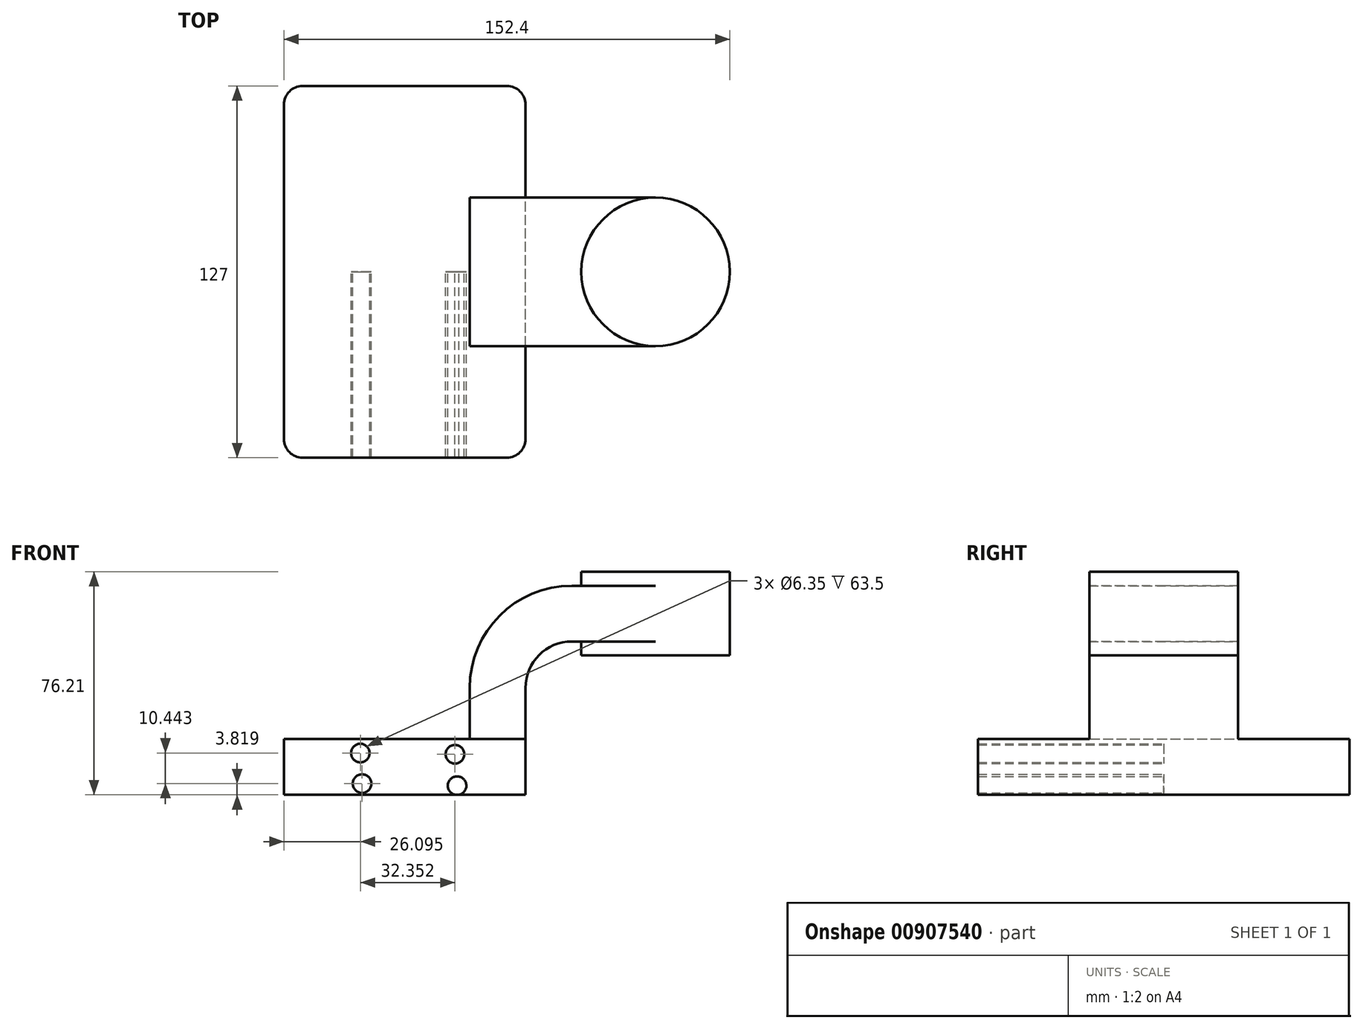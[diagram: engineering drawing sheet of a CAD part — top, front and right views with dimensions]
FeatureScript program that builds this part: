
annotation { "Feature Type Name" : "Feature", "Feature Type Description" : "" }
export const myFeature = defineFeature(function(context is Context, id is Id, definition is map)
    precondition{}
    {
        {
            var Q0;
            Q0=qCreatedBy(makeId("Front.planeOp"),FACE);
            var sketch = newSketch(context, id + "F0", { "sketchPlane" : qUnion([Q0])});
            skLineSegment(sketch, "E0.bottom", {"start": v(41.27, 9.53) * mm, "end": v(-41.28, 9.53) * mm});
            skLineSegment(sketch, "E0.top", {"start": v(41.28, -9.52) * mm, "end": v(-41.27, -9.52) * mm});
            skLineSegment(sketch, "E0.left", {"start": v(41.28, 9.53) * mm, "end": v(41.28, -9.52) * mm});
            skLineSegment(sketch, "E0.right", {"start": v(-41.28, 9.53) * mm, "end": v(-41.27, -9.52) * mm});
            skPoint(sketch, "E0.middle", {"position": v(0, 0) * mm});
            skLineSegment(sketch, "E1.bottom", {"start": v(111.13, 66.68) * mm, "end": v(60.33, 66.68) * mm});
            skLineSegment(sketch, "E1.top", {"start": v(111.13, 38.1) * mm, "end": v(60.33, 38.1) * mm});
            skLineSegment(sketch, "E1.left", {"start": v(111.13, 66.68) * mm, "end": v(111.13, 38.1) * mm});
            skLineSegment(sketch, "E1.right", {"start": v(60.33, 66.68) * mm, "end": v(60.33, 38.1) * mm});
            skPoint(sketch, "E1.middle", {"position": v(85.73, 52.39) * mm});
            skLineSegment(sketch, "E2", {"start": v(41.27, 9.53) * mm, "end": v(41.27, 27) * mm});
            skArc(sketch, "E3", {"start": v(41.27, 27) * mm, "mid": v(45.92, 38.23) * mm, "end": v(57.15, 42.88) * mm});
            skLineSegment(sketch, "E4", {"start": v(57.15, 42.88) * mm, "end": v(85.73, 42.88) * mm});
            skPoint(sketch, "E4.endSnap0", {"position": v(85.73, 38.1) * mm});
            skLineSegment(sketch, "E5.0", {"start": v(57.15, 61.93) * mm, "end": v(85.73, 61.93) * mm});
            skArc(sketch, "E5.1", {"start": v(22.23, 27) * mm, "mid": v(32.45, 51.7) * mm, "end": v(57.15, 61.93) * mm});
            skLineSegment(sketch, "E5.2", {"start": v(22.22, 9.53) * mm, "end": v(22.22, 27) * mm});
            skLineSegment(sketch, "E6", {"start": v(85.73, 38.1) * mm, "end": v(85.73, 66.68) * mm});
            skFitSpline(sketch, "E7", {"points": [v(-41.28, 9.53) * mm, v(57.15, 61.93) * mm], "startDerivative": vector(14.27, 106.94) * mm, "endDerivative": vector(136.15, -6.65) * mm});
            skSolve(sketch);
        }
        {
            var Q0;
            Q0=makeQuery(id+"F0.imprint","IMPRINT",FACE,{"disambiguationData":[TD([[makeQuery(id+"F0.imprint","IMPRINT",EDGE,{"derivedFrom":sQuery(id+"F0.wireOp",EDGE,"E0.top")}),-1.0]])]});
            extrude(context, id + "F1", {"entities" : qUnion([Q0]), "endBound" : BoundingType.SYMMETRIC, "depth" : 127 * mm, "offsetDistance" : 25.4 * mm});
        }
        {
            var Q0;
            {var subQ1=sQuery(id+"F0.wireOp",EDGE,"E2");Q0=makeQuery(id+"F0.imprint","IMPRINT",FACE,{"disambiguationData":[TD([[makeQuery(id+"F0.imprint","IMPRINT",EDGE,{"derivedFrom":subQ1}),1.0]])]});}
            extrude(context, id + "F2", {"entities" : qUnion([Q0]), "operationType" : NewBodyOperationType.ADD, "endBound" : BoundingType.SYMMETRIC, "depth" : 50.8 * mm, "offsetDistance" : 25.4 * mm});
        }
        {
            var Q0;
            {var subQ0=sQuery(id+"F0.wireOp",EDGE,"E5.0");var subQ1=sQuery(id+"F0.wireOp",EDGE,"E1.right");var subQ2=makeQuery(id+"F0.imprint","INTERSECT",VERTEX,{"derivedFrom":[subQ1,subQ0]});Q0=makeQuery(id+"F0.imprint","IMPRINT",FACE,{"disambiguationData":[TD([[makeQuery(id+"F0.imprint","IMPRINT",EDGE,{"disambiguationData":[TD([[subQ2,-1.0]])],"derivedFrom":subQ1}),1.0]])]});}
            extrude(context, id + "F3", {"entities" : qUnion([Q0]), "operationType" : NewBodyOperationType.ADD, "endBound" : BoundingType.SYMMETRIC, "depth" : 50.8 * mm, "offsetDistance" : 25.4 * mm});
        }
        {
            var Q0;
            {var subQ4=sQuery(id+"F0.wireOp",EDGE,"E1.left");Q0=makeQuery(id+"F0.imprint","IMPRINT",FACE,{"disambiguationData":[TD([[makeQuery(id+"F0.imprint","IMPRINT",EDGE,{"derivedFrom":subQ4}),-1.0]])]});}
            var Q1;
            Q1=sQuery(id+"F0.wireOp",EDGE,"E6");
            revolve(context, id + "F4", {"operationType" : NewBodyOperationType.ADD, "surfaceOperationType" : NewSurfaceOperationType.NEW, "entities" : qUnion([Q0]), "axis" : qUnion([Q1]), "revolveType" : RevolveType.FULL});
        }
        {
            var Q0;
            Q0=makeQuery(id+"F1.opExtrude","CAP_EDGE",EDGE,{"disambiguationData":[OSD([sQuery(id+"F0.wireOp",EDGE,"E0.right")])],"isStart":false});
            var Q1;
            Q1=makeQuery(id+"F1.opExtrude","CAP_EDGE",EDGE,{"disambiguationData":[OSD([sQuery(id+"F0.wireOp",EDGE,"E0.left")])],"isStart":false});
            var Q2;
            Q2=makeQuery(id+"F1.opExtrude","CAP_EDGE",EDGE,{"disambiguationData":[OSD([sQuery(id+"F0.wireOp",EDGE,"E0.left")])],"isStart":true});
            var Q3;
            Q3=makeQuery(id+"F1.opExtrude","CAP_EDGE",EDGE,{"disambiguationData":[OSD([sQuery(id+"F0.wireOp",EDGE,"E0.right")])],"isStart":true});
            fillet(context, id + "F5", {"entities" : qUnion([Q0, Q1, Q2, Q3]), "radius" : 6.35 * mm, "tangentPropagation" : true, "allowEdgeOverflow" : false});
        }
        {
            var Q0;
            Q0=qCreatedBy(makeId("Front.planeOp"),FACE);
            var sketch = newSketch(context, id + "F6", { "sketchPlane" : qUnion([Q0])});
            skPoint(sketch, "E8", {"position": v(17.18, 4.32) * mm});
            skPoint(sketch, "E9", {"position": v(-15.17, 4.73) * mm});
            skPoint(sketch, "E10", {"position": v(17.9, -6.43) * mm});
            skPoint(sketch, "E11", {"position": v(-14.56, -5.71) * mm});
            skSolve(sketch);
        }
        {
            var Q0;
            Q0=sQuery(id+"F6.wireOp",VERTEX,"E8");
            var Q1;
            Q1=sQuery(id+"F6.wireOp",VERTEX,"E9");
            var Q2;
            Q2=sQuery(id+"F6.wireOp",VERTEX,"E11");
            var Q3;
            Q3=sQuery(id+"F6.wireOp",VERTEX,"E10");
            var Q4;
            Q4=makeQuery(id+"F1.opExtrude","SWEPT_BODY",BODY,{"disambiguationData":[OSD([sQuery(id+"F0.wireOp",EDGE,"E0.bottom"),sQuery(id+"F0.wireOp",EDGE,"E0.top"),sQuery(id+"F0.wireOp",EDGE,"E0.left"),sQuery(id+"F0.wireOp",EDGE,"E0.right")])]});
            hole(context, id + "F7", {"style" : HoleStyle.SIMPLE, "endStyle" : HoleEndStyle.THROUGH, "oppositeDirection" : true, "holeDiameter" : 6.35 * mm, "majorDiameter" : 6.35 * mm, "isTappedThrough" : true, "tappedDepth" : 12.7 * mm, "tapClearance" : 3, "locations" : qUnion([Q0, Q1, Q2, Q3]), "scope" : qUnion([Q4])});
        }
    });
